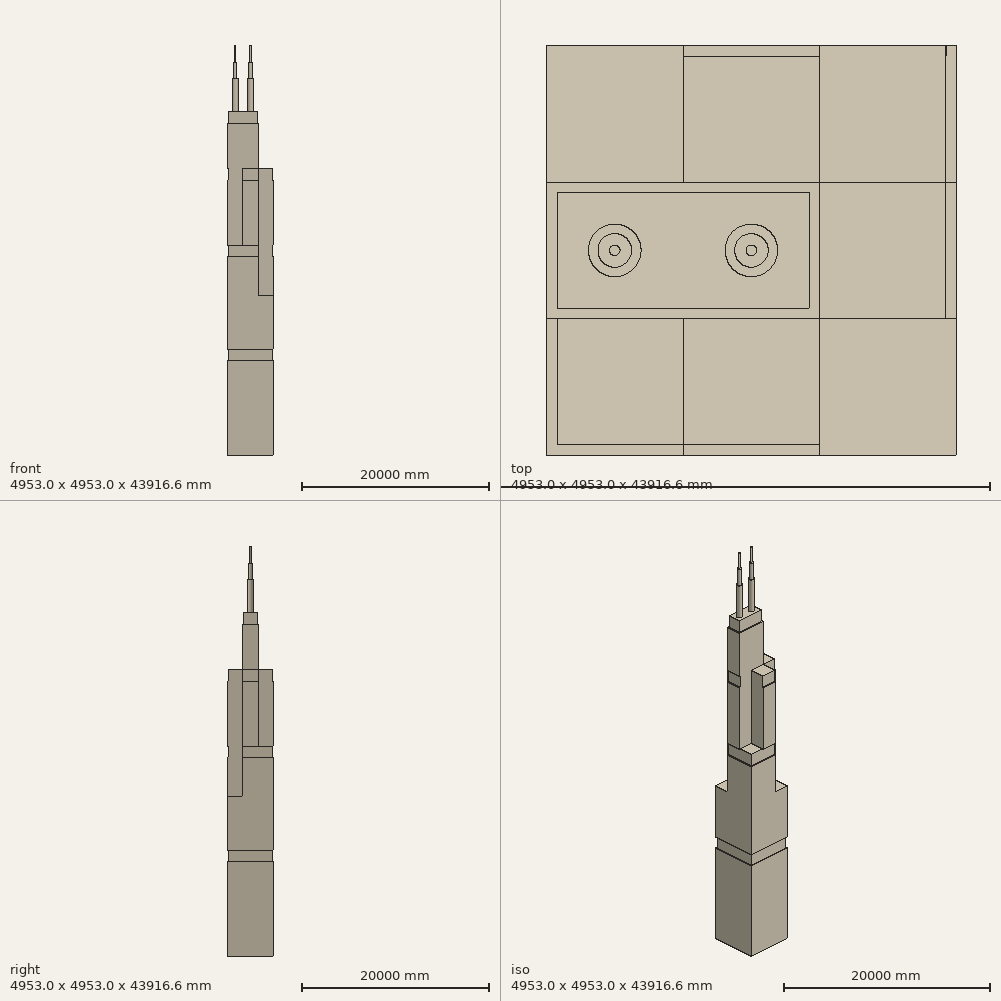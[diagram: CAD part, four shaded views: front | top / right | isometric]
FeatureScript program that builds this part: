
annotation { "Feature Type Name" : "Feature", "Feature Type Description" : "" }
export const myFeature = defineFeature(function(context is Context, id is Id, definition is map)
    precondition{}
    {
        {
            var Q0;
            Q0=qCreatedBy(makeId("Top.planeOp"),FACE);
            var sketch = newSketch(context, id + "F0", { "sketchPlane" : qUnion([Q0])});
            skLineSegment(sketch, "E0.bottom", {"start": v(-2636.4, 2535.41) * mm, "end": v(2316.6, 2535.41) * mm});
            skLineSegment(sketch, "E0.top", {"start": v(-2636.4, -2417.59) * mm, "end": v(2316.6, -2417.59) * mm});
            skLineSegment(sketch, "E0.left", {"start": v(-2636.4, 2535.41) * mm, "end": v(-2636.4, -2417.59) * mm});
            skLineSegment(sketch, "E0.right", {"start": v(2316.6, 2535.41) * mm, "end": v(2316.6, -2417.59) * mm});
            skLineSegment(sketch, "E1", {"start": v(-985.4, 2535.41) * mm, "end": v(-985.4, -2417.59) * mm});
            skLineSegment(sketch, "E2", {"start": v(665.6, 2535.41) * mm, "end": v(665.6, -2417.59) * mm});
            skLineSegment(sketch, "E3", {"start": v(-2636.4, 884.41) * mm, "end": v(2316.6, 884.41) * mm});
            skLineSegment(sketch, "E4", {"start": v(-2636.4, -766.59) * mm, "end": v(2316.6, -766.59) * mm});
            skSolve(sketch);
        }
        {
            var Q0;
            Q0 = qSketchRegion(id + "F0", true);
            var Q1;
            {var subQ0=sQuery(id+"F0.wireOp",EDGE,"E3");var subQ1=sQuery(id+"F0.wireOp",EDGE,"E1");var subQ2=makeQuery(id+"F0.imprint","INTERSECT",VERTEX,{"derivedFrom":[subQ1,subQ0]});Q1=makeQuery(id+"F0.imprint","IMPRINT",FACE,{"disambiguationData":[TD([[makeQuery(id+"F0.imprint","IMPRINT",EDGE,{"disambiguationData":[TD([[subQ2,-1.0]])],"derivedFrom":subQ1}),1.0]])]});}
            extrude(context, id + "F1", {"entities" : qUnion([Q0, Q1]), "depth" : 36830 * mm, "offsetDistance" : 25.4 * mm});
        }
        {
            var Q0;
            Q0=makeQuery(id+"F1.opExtrude","CAP_FACE",FACE,{"disambiguationData":[OSD([sQuery(id+"F0.wireOp",EDGE,"E0.bottom"),sQuery(id+"F0.wireOp",EDGE,"E0.top"),sQuery(id+"F0.wireOp",EDGE,"E0.left"),sQuery(id+"F0.wireOp",EDGE,"E0.right")])],"isStart":false});
            var sketch = newSketch(context, id + "F2", { "sketchPlane" : qUnion([Q0])});
            skLineSegment(sketch, "E5.0", {"start": v(-985.4, 2535.41) * mm, "end": v(-985.4, -2417.59) * mm});
            skLineSegment(sketch, "E6.0", {"start": v(665.6, 2535.41) * mm, "end": v(665.6, -2417.59) * mm});
            skLineSegment(sketch, "E7.0", {"start": v(-2636.4, -766.59) * mm, "end": v(2316.6, -766.59) * mm});
            skLineSegment(sketch, "E8.0", {"start": v(-2636.4, 884.41) * mm, "end": v(2316.6, 884.41) * mm});
            skLineSegment(sketch, "E9", {"start": v(2316.6, -2417.59) * mm, "end": v(-2636.4, -2417.59) * mm});
            skLineSegment(sketch, "E10", {"start": v(-2636.4, -2417.59) * mm, "end": v(-2636.4, 2535.41) * mm});
            skLineSegment(sketch, "E11", {"start": v(-2636.4, 2535.41) * mm, "end": v(2316.6, 2535.41) * mm});
            skLineSegment(sketch, "E12", {"start": v(2316.6, 2535.41) * mm, "end": v(2316.6, -2417.59) * mm});
            skSolve(sketch);
        }
        {
            var Q0;
            {var subQ0=sQuery(id+"F2.wireOp",EDGE,"E11");var subQ1=sQuery(id+"F2.wireOp",EDGE,"E5.0");var subQ2=makeQuery(id+"F2.imprint","INTERSECT",VERTEX,{"derivedFrom":[subQ1,subQ0]});Q0=makeQuery(id+"F2.imprint","IMPRINT",FACE,{"disambiguationData":[TD([[makeQuery(id+"F2.imprint","IMPRINT",EDGE,{"disambiguationData":[TD([[subQ2,-1.0]])],"derivedFrom":subQ1}),-1.0]])]});}
            var Q1;
            {var subQ0=sQuery(id+"F2.wireOp",EDGE,"E9");var subQ1=sQuery(id+"F2.wireOp",EDGE,"E6.0");var subQ2=makeQuery(id+"F2.imprint","INTERSECT",VERTEX,{"derivedFrom":[subQ1,subQ0]});Q1=makeQuery(id+"F2.imprint","IMPRINT",FACE,{"disambiguationData":[TD([[makeQuery(id+"F2.imprint","IMPRINT",EDGE,{"disambiguationData":[TD([[subQ2,1.0]])],"derivedFrom":subQ1}),1.0]])]});}
            extrude(context, id + "F3", {"entities" : qUnion([Q0, Q1]), "operationType" : NewBodyOperationType.REMOVE, "oppositeDirection" : true, "depth" : 19740.88 * mm, "offsetDistance" : 25.4 * mm});
        }
        {
            var Q0;
            {var subQ0=sQuery(id+"F2.wireOp",EDGE,"E9");var subQ1=sQuery(id+"F2.wireOp",EDGE,"E5.0");var subQ2=makeQuery(id+"F2.imprint","INTERSECT",VERTEX,{"derivedFrom":[subQ1,subQ0]});Q0=makeQuery(id+"F2.imprint","IMPRINT",FACE,{"disambiguationData":[TD([[makeQuery(id+"F2.imprint","IMPRINT",EDGE,{"disambiguationData":[TD([[subQ2,1.0]])],"derivedFrom":subQ1}),-1.0]])]});}
            var Q1;
            {var subQ0=sQuery(id+"F2.wireOp",EDGE,"E11");var subQ1=sQuery(id+"F2.wireOp",EDGE,"E6.0");var subQ2=makeQuery(id+"F2.imprint","INTERSECT",VERTEX,{"derivedFrom":[subQ1,subQ0]});Q1=makeQuery(id+"F2.imprint","IMPRINT",FACE,{"disambiguationData":[TD([[makeQuery(id+"F2.imprint","IMPRINT",EDGE,{"disambiguationData":[TD([[subQ2,-1.0]])],"derivedFrom":subQ1}),1.0]])]});}
            extrude(context, id + "F4", {"entities" : qUnion([Q0, Q1]), "operationType" : NewBodyOperationType.REMOVE, "oppositeDirection" : true, "depth" : 14295.12 * mm, "offsetDistance" : 25.4 * mm});
        }
        {
            var Q0;
            {var subQ0=sQuery(id+"F2.wireOp",EDGE,"E11");var subQ1=sQuery(id+"F2.wireOp",EDGE,"E5.0");var subQ2=makeQuery(id+"F2.imprint","INTERSECT",VERTEX,{"derivedFrom":[subQ1,subQ0]});Q0=makeQuery(id+"F2.imprint","IMPRINT",FACE,{"disambiguationData":[TD([[makeQuery(id+"F2.imprint","IMPRINT",EDGE,{"disambiguationData":[TD([[subQ2,-1.0]])],"derivedFrom":subQ1}),1.0]])]});}
            var Q1;
            {var subQ0=sQuery(id+"F2.wireOp",EDGE,"E8.0");var subQ1=sQuery(id+"F2.wireOp",EDGE,"E6.0");var subQ2=makeQuery(id+"F2.imprint","INTERSECT",VERTEX,{"derivedFrom":[subQ1,subQ0]});Q1=makeQuery(id+"F2.imprint","IMPRINT",FACE,{"disambiguationData":[TD([[makeQuery(id+"F2.imprint","IMPRINT",EDGE,{"disambiguationData":[TD([[subQ2,-1.0]])],"derivedFrom":subQ1}),1.0]])]});}
            var Q2;
            {var subQ0=sQuery(id+"F2.wireOp",EDGE,"E9");var subQ1=sQuery(id+"F2.wireOp",EDGE,"E5.0");var subQ2=makeQuery(id+"F2.imprint","INTERSECT",VERTEX,{"derivedFrom":[subQ1,subQ0]});Q2=makeQuery(id+"F2.imprint","IMPRINT",FACE,{"disambiguationData":[TD([[makeQuery(id+"F2.imprint","IMPRINT",EDGE,{"disambiguationData":[TD([[subQ2,1.0]])],"derivedFrom":subQ1}),1.0]])]});}
            extrude(context, id + "F5", {"entities" : qUnion([Q0, Q1, Q2]), "operationType" : NewBodyOperationType.REMOVE, "oppositeDirection" : true, "depth" : 6126.48 * mm, "offsetDistance" : 25.4 * mm});
        }
        {
            var Q0;
            Q0=makeQuery(id+"F1.opExtrude","CAP_FACE",FACE,{"disambiguationData":[OSD([sQuery(id+"F0.wireOp",EDGE,"E0.bottom"),sQuery(id+"F0.wireOp",EDGE,"E0.top"),sQuery(id+"F0.wireOp",EDGE,"E0.left"),sQuery(id+"F0.wireOp",EDGE,"E0.right")])],"isStart":false});
            var sketch = newSketch(context, id + "F6", { "sketchPlane" : qUnion([Q0])});
            skCircle(sketch, "E13", {"center": v(-159.9, 58.91) * mm, "radius": 317.5 * mm});
            skPoint(sketch, "E13.centerSnap0", {"position": v(-159.9, 58.91) * mm});
            skCircle(sketch, "E14", {"center": v(-1810.9, 58.91) * mm, "radius": 317.5 * mm});
            skSolve(sketch);
        }
        {
            var Q0;
            Q0 = qSketchRegion(id + "F6", true);
            extrude(context, id + "F7", {"entities" : qUnion([Q0]), "operationType" : NewBodyOperationType.ADD, "depth" : 3543.3 * mm, "offsetDistance" : 25.4 * mm});
        }
        {
            var Q0;
            Q0=makeQuery(id+"F7.opExtrude","CAP_FACE",FACE,{"disambiguationData":[OSD([sQuery(id+"F6.wireOp",EDGE,"E14")])],"isStart":false});
            var sketch = newSketch(context, id + "F8", { "sketchPlane" : qUnion([Q0])});
            skCircle(sketch, "E15", {"center": v(-1810.9, 58.91) * mm, "radius": 203.2 * mm});
            skCircle(sketch, "E16", {"center": v(-159.9, 58.91) * mm, "radius": 203.2 * mm});
            skSolve(sketch);
        }
        {
            var Q0;
            Q0 = qSketchRegion(id + "F8", true);
            extrude(context, id + "F9", {"entities" : qUnion([Q0]), "operationType" : NewBodyOperationType.ADD, "depth" : 1771.65 * mm, "offsetDistance" : 25.4 * mm});
        }
        {
            var Q0;
            Q0=makeQuery(id+"F9.opExtrude","CAP_FACE",FACE,{"disambiguationData":[OSD([sQuery(id+"F8.wireOp",EDGE,"E16")])],"isStart":false});
            var sketch = newSketch(context, id + "F10", { "sketchPlane" : qUnion([Q0])});
            skCircle(sketch, "E17", {"center": v(-1810.9, 58.91) * mm, "radius": 63.5 * mm});
            skCircle(sketch, "E18", {"center": v(-159.9, 58.91) * mm, "radius": 63.5 * mm});
            skSolve(sketch);
        }
        {
            var Q0;
            Q0 = qSketchRegion(id + "F10", true);
            extrude(context, id + "F11", {"entities" : qUnion([Q0]), "operationType" : NewBodyOperationType.ADD, "depth" : 1771.65 * mm, "offsetDistance" : 25.4 * mm});
        }
        {
            var Q0;
            Q0=makeQuery(id+"F1.opExtrude","SWEPT_FACE",FACE,{"disambiguationData":[OSD([sQuery(id+"F0.wireOp",EDGE,"E0.top")])]});
            var sketch = newSketch(context, id + "F12", { "sketchPlane" : qUnion([Q0])});
            skLineSegment(sketch, "E19", {"start": v(2316.6, 17089.12) * mm, "end": v(2316.6, 0) * mm});
            skLineSegment(sketch, "E20", {"start": v(2316.6, 11392.66) * mm, "end": v(-2636.4, 11392.66) * mm});
            skLineSegment(sketch, "E21", {"start": v(-2636.4, 10122.66) * mm, "end": v(2316.6, 10122.66) * mm});
            skLineSegment(sketch, "E22", {"start": v(665.6, 30703.52) * mm, "end": v(665.6, 17089.12) * mm});
            skLineSegment(sketch, "E23", {"start": v(-2636.4, 22534.88) * mm, "end": v(665.6, 22534.88) * mm});
            skLineSegment(sketch, "E24", {"start": v(665.6, 21264.88) * mm, "end": v(-2636.4, 21264.88) * mm});
            skLineSegment(sketch, "E25", {"start": v(-985.4, 29433.52) * mm, "end": v(665.6, 29433.52) * mm});
            skSolve(sketch);
        }
        {
            var Q0;
            {var subQ0=sQuery(id+"F2.wireOp",EDGE,"E7.0");Q0=makeQuery(id+"F5.boolean.opBoolean","MERGE",FACE,{"derivedFrom":[makeQuery(id+"F4.boolean.opBoolean","COPY",FACE,{"derivedFrom":makeQuery(id+"F4.opExtrude","SWEPT_FACE",FACE,{"disambiguationData":[OSD([subQ0])]})})],"fromTools":[makeQuery(id+"F5.opExtrude","SWEPT_FACE",FACE,{"disambiguationData":[OSD([subQ0]),TDD([makeQuery(id+"F2.imprint","IMPRINT",EDGE,{"disambiguationData":[TD([[makeQuery(id+"F2.imprint","INTERSECT",VERTEX,{"derivedFrom":[sQuery(id+"F2.wireOp",EDGE,"E5.0"),subQ0]}),-1.0]])],"derivedFrom":subQ0})])]})]});}
            var sketch = newSketch(context, id + "F13", { "sketchPlane" : qUnion([Q0])});
            skLineSegment(sketch, "E26", {"start": v(-2636.4, 35560) * mm, "end": v(665.6, 35560) * mm});
            skSolve(sketch);
        }
        {
            var Q0;
            Q0=makeQuery(id+"F1.opExtrude","SWEPT_FACE",FACE,{"disambiguationData":[OSD([sQuery(id+"F0.wireOp",EDGE,"E0.left")])]});
            var sketch = newSketch(context, id + "F14", { "sketchPlane" : qUnion([Q0])});
            skPoint(sketch, "E27.0", {"position": v(766.59, 36830) * mm});
            skPoint(sketch, "E28.0", {"position": v(766.59, 35560) * mm});
            skPoint(sketch, "E29.0", {"position": v(2417.59, 30703.52) * mm});
            skPoint(sketch, "E30.0", {"position": v(2417.59, 29433.52) * mm});
            skPoint(sketch, "E31.0", {"position": v(2417.59, 22534.88) * mm});
            skPoint(sketch, "E32.0", {"position": v(2417.59, 21264.88) * mm});
            skPoint(sketch, "E33.0", {"position": v(2417.59, 11392.66) * mm});
            skPoint(sketch, "E34.0", {"position": v(2417.59, 10122.66) * mm});
            skLineSegment(sketch, "E35", {"start": v(766.59, 36830) * mm, "end": v(-884.41, 36830) * mm});
            skLineSegment(sketch, "E36", {"start": v(766.59, 35560) * mm, "end": v(-884.41, 35560) * mm});
            skLineSegment(sketch, "E37", {"start": v(-884.41, 35560) * mm, "end": v(-884.41, 36830) * mm});
            skLineSegment(sketch, "E38", {"start": v(766.59, 36830) * mm, "end": v(766.59, 35560) * mm});
            skLineSegment(sketch, "E39", {"start": v(766.59, 30703.52) * mm, "end": v(-884.41, 30703.52) * mm});
            skLineSegment(sketch, "E40", {"start": v(766.59, 29433.52) * mm, "end": v(-884.41, 29433.52) * mm});
            skLineSegment(sketch, "E41", {"start": v(2417.59, 22534.88) * mm, "end": v(-884.41, 22534.88) * mm});
            skLineSegment(sketch, "E42", {"start": v(2417.59, 21264.88) * mm, "end": v(-884.41, 21264.88) * mm});
            skLineSegment(sketch, "E43", {"start": v(2417.59, 11392.66) * mm, "end": v(-2535.41, 11392.66) * mm});
            skLineSegment(sketch, "E44", {"start": v(2417.59, 10122.66) * mm, "end": v(-2535.41, 10122.66) * mm});
            skSolve(sketch);
        }
        {
            var Q0;
            Q0=makeQuery(id+"F1.opExtrude","SWEPT_FACE",FACE,{"disambiguationData":[OSD([sQuery(id+"F0.wireOp",EDGE,"E0.bottom")])]});
            var sketch = newSketch(context, id + "F15", { "sketchPlane" : qUnion([Q0])});
            skLineSegment(sketch, "E45", {"start": v(985.4, 22528) * mm, "end": v(-2316.6, 22534.88) * mm});
            skPoint(sketch, "E46.0", {"position": v(-665.6, 21264.88) * mm});
            skLineSegment(sketch, "E47", {"start": v(985.4, 21264.88) * mm, "end": v(-2316.6, 21264.88) * mm});
            skLineSegment(sketch, "E48.0", {"start": v(985.4, 29433.52) * mm, "end": v(-665.6, 29433.52) * mm});
            skLineSegment(sketch, "E49.0", {"start": v(2636.4, 10122.66) * mm, "end": v(-2316.6, 10122.66) * mm});
            skLineSegment(sketch, "E50.0", {"start": v(-2316.6, 11392.66) * mm, "end": v(2636.4, 11392.66) * mm});
            skSolve(sketch);
        }
        {
            var Q0;
            {var subQ0=sQuery(id+"F2.wireOp",EDGE,"E8.0");Q0=makeQuery(id+"F5.boolean.opBoolean","MERGE",FACE,{"derivedFrom":[makeQuery(id+"F3.boolean.opBoolean","COPY",FACE,{"derivedFrom":makeQuery(id+"F3.opExtrude","SWEPT_FACE",FACE,{"disambiguationData":[OSD([subQ0])]})})],"fromTools":[makeQuery(id+"F5.opExtrude","SWEPT_FACE",FACE,{"disambiguationData":[OSD([subQ0]),TDD([makeQuery(id+"F2.imprint","IMPRINT",EDGE,{"disambiguationData":[TD([[makeQuery(id+"F2.imprint","INTERSECT",VERTEX,{"derivedFrom":[sQuery(id+"F2.wireOp",EDGE,"E5.0"),subQ0]}),-1.0]])],"derivedFrom":subQ0})])]})]});}
            var sketch = newSketch(context, id + "F16", { "sketchPlane" : qUnion([Q0])});
            skLineSegment(sketch, "E51.0", {"start": v(2636.4, 35560) * mm, "end": v(-665.6, 35560) * mm});
            skSolve(sketch);
        }
        {
            var Q0;
            Q0=makeQuery(id+"F1.opExtrude","SWEPT_FACE",FACE,{"disambiguationData":[OSD([sQuery(id+"F0.wireOp",EDGE,"E0.right")])]});
            var sketch = newSketch(context, id + "F17", { "sketchPlane" : qUnion([Q0])});
            skLineSegment(sketch, "E52.0", {"start": v(-766.59, 29433.52) * mm, "end": v(884.41, 29433.52) * mm});
            skPoint(sketch, "E53.0", {"position": v(884.41, 21264.88) * mm});
            skLineSegment(sketch, "E54", {"start": v(-766.59, 22534.88) * mm, "end": v(2535.41, 22534.88) * mm});
            skLineSegment(sketch, "E55", {"start": v(-766.59, 21264.88) * mm, "end": v(2535.41, 21264.88) * mm});
            skLineSegment(sketch, "E56.0", {"start": v(-2417.59, 11392.66) * mm, "end": v(2535.41, 11392.66) * mm});
            skLineSegment(sketch, "E57.0", {"start": v(-2417.59, 10122.66) * mm, "end": v(2535.41, 10122.66) * mm});
            skSolve(sketch);
        }
        {
            var Q0;
            {var subQ0=sQuery(id+"F2.wireOp",EDGE,"E6.0");Q0=makeQuery(id+"F5.boolean.opBoolean","MERGE",FACE,{"disambiguationData":[OD(2.0)],"derivedFrom":[makeQuery(id+"F3.boolean.opBoolean","COPY",FACE,{"derivedFrom":makeQuery(id+"F3.opExtrude","SWEPT_FACE",FACE,{"disambiguationData":[OSD([subQ0])]})}),makeQuery(id+"F4.boolean.opBoolean","COPY",FACE,{"derivedFrom":makeQuery(id+"F4.opExtrude","SWEPT_FACE",FACE,{"disambiguationData":[OSD([subQ0])]})})],"fromTools":[makeQuery(id+"F5.opExtrude","SWEPT_FACE",FACE,{"disambiguationData":[OSD([subQ0]),TDD([makeQuery(id+"F2.imprint","IMPRINT",EDGE,{"disambiguationData":[TD([[makeQuery(id+"F2.imprint","INTERSECT",VERTEX,{"derivedFrom":[subQ0,sQuery(id+"F2.wireOp",EDGE,"E8.0")]}),-1.0]])],"derivedFrom":subQ0})])]})]});}
            var sketch = newSketch(context, id + "F18", { "sketchPlane" : qUnion([Q0])});
            skLineSegment(sketch, "E58.0", {"start": v(-766.59, 35560) * mm, "end": v(884.41, 35560) * mm});
            skSolve(sketch);
        }
        {
            var Q0;
            {var subQ0=sQuery(id+"F13.wireOp",EDGE,"E26");Q0=makeQuery(id+"F13.imprint","IMPRINT",FACE,{"disambiguationData":[TD([[makeQuery(id+"F13.imprint","IMPRINT",EDGE,{"derivedFrom":subQ0}),1.0]])]});}
            var Q1;
            {var subQ3=sQuery(id+"F12.wireOp",EDGE,"E25");Q1=makeQuery(id+"F12.imprint","IMPRINT",FACE,{"disambiguationData":[TD([[makeQuery(id+"F12.imprint","IMPRINT",EDGE,{"derivedFrom":subQ3}),1.0]])]});}
            var Q2;
            {var subQ6=sQuery(id+"F12.wireOp",EDGE,"E24");Q2=makeQuery(id+"F12.imprint","IMPRINT",FACE,{"disambiguationData":[TD([[makeQuery(id+"F12.imprint","IMPRINT",EDGE,{"derivedFrom":subQ6}),-1.0]])]});}
            var Q3;
            {var subQ0=sQuery(id+"F12.wireOp",EDGE,"E20");Q3=makeQuery(id+"F12.imprint","IMPRINT",FACE,{"disambiguationData":[TD([[makeQuery(id+"F12.imprint","IMPRINT",EDGE,{"derivedFrom":subQ0}),1.0]])]});}
            extrude(context, id + "F19", {"entities" : qUnion([Q0, Q1, Q2, Q3]), "operationType" : NewBodyOperationType.REMOVE, "oppositeDirection" : true, "depth" : 127 * mm, "offsetDistance" : 25.4 * mm});
        }
        {
            var Q0;
            Q0=makeQuery(id+"F14.imprint","IMPRINT",FACE,{"disambiguationData":[TD([[makeQuery(id+"F14.imprint","IMPRINT",EDGE,{"derivedFrom":sQuery(id+"F14.wireOp",EDGE,"E35")}),-1.0]])]});
            var Q1;
            {var subQ0=sQuery(id+"F14.wireOp",EDGE,"E39");Q1=makeQuery(id+"F14.imprint","IMPRINT",FACE,{"disambiguationData":[TD([[makeQuery(id+"F14.imprint","IMPRINT",EDGE,{"derivedFrom":subQ0}),1.0]])]});}
            var Q2;
            {var subQ0=sQuery(id+"F14.wireOp",EDGE,"E42");Q2=makeQuery(id+"F14.imprint","IMPRINT",FACE,{"disambiguationData":[TD([[makeQuery(id+"F14.imprint","IMPRINT",EDGE,{"derivedFrom":subQ0}),-1.0]])]});}
            var Q3;
            {var subQ0=sQuery(id+"F14.wireOp",EDGE,"E43");Q3=makeQuery(id+"F14.imprint","IMPRINT",FACE,{"disambiguationData":[TD([[makeQuery(id+"F14.imprint","IMPRINT",EDGE,{"derivedFrom":subQ0}),1.0]])]});}
            extrude(context, id + "F20", {"entities" : qUnion([Q0, Q1, Q2, Q3]), "operationType" : NewBodyOperationType.REMOVE, "oppositeDirection" : true, "depth" : 127 * mm, "offsetDistance" : 25.4 * mm});
        }
        {
            var Q0;
            {var subQ0=sQuery(id+"F16.wireOp",EDGE,"E51.0");Q0=makeQuery(id+"F16.imprint","IMPRINT",FACE,{"disambiguationData":[TD([[makeQuery(id+"F16.imprint","IMPRINT",EDGE,{"derivedFrom":subQ0}),-1.0]])]});}
            var Q1;
            {var subQ0=sQuery(id+"F15.wireOp",EDGE,"E48.0");Q1=makeQuery(id+"F15.imprint","IMPRINT",FACE,{"disambiguationData":[TD([[makeQuery(id+"F15.imprint","IMPRINT",EDGE,{"derivedFrom":subQ0}),-1.0]])]});}
            var Q2;
            {var subQ0=sQuery(id+"F15.wireOp",EDGE,"E45");Q2=makeQuery(id+"F15.imprint","IMPRINT",FACE,{"disambiguationData":[TD([[makeQuery(id+"F15.imprint","IMPRINT",EDGE,{"derivedFrom":subQ0}),1.0]])]});}
            var Q3;
            {var subQ0=sQuery(id+"F15.wireOp",EDGE,"E49.0");Q3=makeQuery(id+"F15.imprint","IMPRINT",FACE,{"disambiguationData":[TD([[makeQuery(id+"F15.imprint","IMPRINT",EDGE,{"derivedFrom":subQ0}),-1.0]])]});}
            extrude(context, id + "F21", {"entities" : qUnion([Q0, Q1, Q2, Q3]), "operationType" : NewBodyOperationType.REMOVE, "oppositeDirection" : true, "depth" : 127 * mm, "offsetDistance" : 25.4 * mm});
        }
        {
            var Q0;
            {var subQ0=sQuery(id+"F18.wireOp",EDGE,"E58.0");Q0=makeQuery(id+"F18.imprint","IMPRINT",FACE,{"disambiguationData":[TD([[makeQuery(id+"F18.imprint","IMPRINT",EDGE,{"derivedFrom":subQ0}),1.0]])]});}
            var Q1;
            {var subQ0=sQuery(id+"F17.wireOp",EDGE,"E52.0");Q1=makeQuery(id+"F17.imprint","IMPRINT",FACE,{"disambiguationData":[TD([[makeQuery(id+"F17.imprint","IMPRINT",EDGE,{"derivedFrom":subQ0}),1.0]])]});}
            var Q2;
            {var subQ3=sQuery(id+"F17.wireOp",EDGE,"E55");Q2=makeQuery(id+"F17.imprint","IMPRINT",FACE,{"disambiguationData":[TD([[makeQuery(id+"F17.imprint","IMPRINT",EDGE,{"derivedFrom":subQ3}),1.0]])]});}
            var Q3;
            {var subQ0=sQuery(id+"F17.wireOp",EDGE,"E56.0");Q3=makeQuery(id+"F17.imprint","IMPRINT",FACE,{"disambiguationData":[TD([[makeQuery(id+"F17.imprint","IMPRINT",EDGE,{"derivedFrom":subQ0}),-1.0]])]});}
            extrude(context, id + "F22", {"entities" : qUnion([Q0, Q1, Q2, Q3]), "operationType" : NewBodyOperationType.REMOVE, "oppositeDirection" : true, "depth" : 127 * mm, "offsetDistance" : 25.4 * mm});
        }
    });
